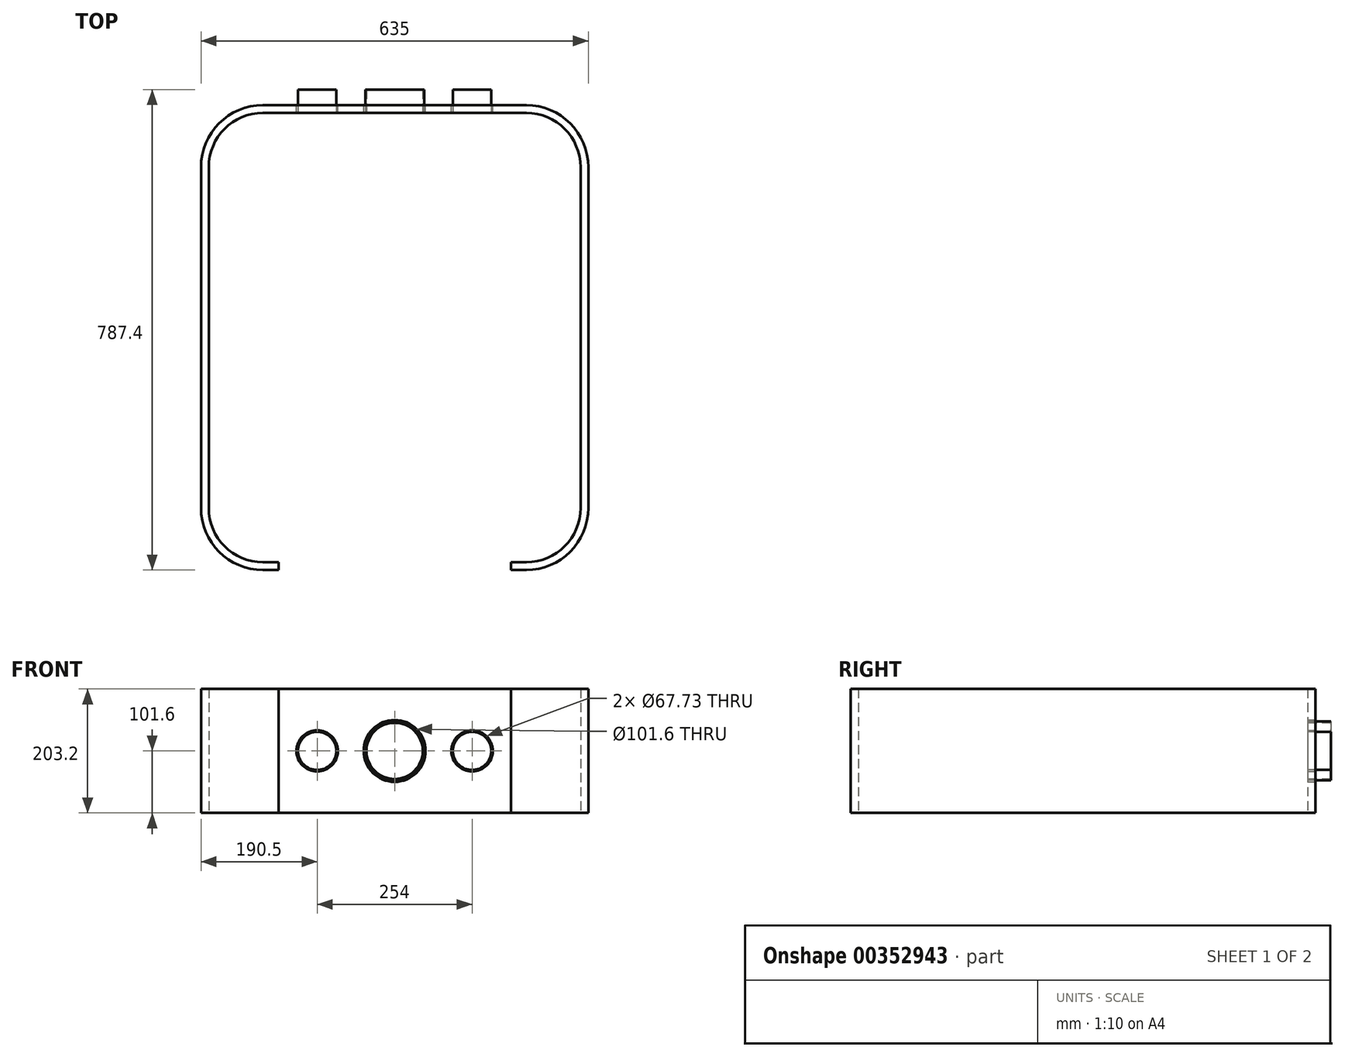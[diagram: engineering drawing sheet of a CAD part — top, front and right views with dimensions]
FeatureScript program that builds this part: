
annotation { "Feature Type Name" : "Feature", "Feature Type Description" : "" }
export const myFeature = defineFeature(function(context is Context, id is Id, definition is map)
    precondition{}
    {
        {
            var Q0;
            Q0=qCreatedBy(makeId("Top.planeOp"),FACE);
            var sketch = newSketch(context, id + "F0", { "sketchPlane" : qUnion([Q0])});
            skLineSegment(sketch, "E0.bottom", {"start": v(-215.9, -381) * mm, "end": v(-190.5, -381) * mm});
            skLineSegment(sketch, "E0.top", {"start": v(-215.9, 381) * mm, "end": v(215.9, 381) * mm});
            skLineSegment(sketch, "E0.left", {"start": v(-317.5, -279.4) * mm, "end": v(-317.5, 279.4) * mm});
            skLineSegment(sketch, "E0.right", {"start": v(317.5, -279.4) * mm, "end": v(317.5, 279.4) * mm});
            skPoint(sketch, "E0.middle", {"position": v(0, 0) * mm});
            skPoint(sketch, "E1.visualSharp", {"position": v(-317.5, 381) * mm});
            skArc(sketch, "E1.filletArc", {"start": v(-215.9, 381) * mm, "mid": v(-287.74, 351.24) * mm, "end": v(-317.5, 279.4) * mm});
            skPoint(sketch, "E2.visualSharp", {"position": v(317.5, 381) * mm});
            skArc(sketch, "E2.filletArc", {"start": v(317.5, 279.4) * mm, "mid": v(287.74, 351.24) * mm, "end": v(215.9, 381) * mm});
            skPoint(sketch, "E3.visualSharp", {"position": v(-317.5, -381) * mm});
            skArc(sketch, "E3.filletArc", {"start": v(-317.5, -279.4) * mm, "mid": v(-287.74, -351.24) * mm, "end": v(-215.9, -381) * mm});
            skPoint(sketch, "E4.visualSharp", {"position": v(317.5, -381) * mm});
            skArc(sketch, "E4.filletArc", {"start": v(215.9, -381) * mm, "mid": v(287.74, -351.24) * mm, "end": v(317.5, -279.4) * mm});
            skArc(sketch, "E5.0", {"start": v(215.9, -368.3) * mm, "mid": v(278.76, -342.26) * mm, "end": v(304.8, -279.4) * mm});
            skLineSegment(sketch, "E5.1", {"start": v(-215.9, -368.3) * mm, "end": v(-190.5, -368.3) * mm});
            skLineSegment(sketch, "E5.2", {"start": v(304.8, -279.4) * mm, "end": v(304.8, 279.4) * mm});
            skArc(sketch, "E5.3", {"start": v(-304.8, -279.4) * mm, "mid": v(-278.76, -342.26) * mm, "end": v(-215.9, -368.3) * mm});
            skArc(sketch, "E5.4", {"start": v(304.8, 279.4) * mm, "mid": v(278.76, 342.26) * mm, "end": v(215.9, 368.3) * mm});
            skLineSegment(sketch, "E5.5", {"start": v(-215.9, 368.3) * mm, "end": v(215.9, 368.3) * mm});
            skArc(sketch, "E5.6", {"start": v(-215.9, 368.3) * mm, "mid": v(-278.76, 342.26) * mm, "end": v(-304.8, 279.4) * mm});
            skLineSegment(sketch, "E5.7", {"start": v(-304.8, -279.4) * mm, "end": v(-304.8, 279.4) * mm});
            skLineSegment(sketch, "E6", {"start": v(-190.5, -368.3) * mm, "end": v(-190.5, -381) * mm});
            skLineSegment(sketch, "E7", {"start": v(0, 633.72) * mm, "end": v(0, -676.93) * mm, "construction": true});
            skPoint(sketch, "E7.endSnap0", {"position": v(0, -381) * mm});
            skLineSegment(sketch, "E8.MirrorCS", {"start": v(190.5, -368.3) * mm, "end": v(190.5, -381) * mm});
            skLineSegment(sketch, "E9.trimOffspring", {"start": v(190.5, -381) * mm, "end": v(215.9, -381) * mm});
            skLineSegment(sketch, "E10.trimOffspring", {"start": v(190.5, -368.3) * mm, "end": v(215.9, -368.3) * mm});
            skSolve(sketch);
        }
        {
            var Q0;
            Q0 = qSketchRegion(id + "F0", true);
            extrude(context, id + "F1", {"entities" : qUnion([Q0]), "depth" : 101.6 * mm, "hasSecondDirection" : true, "secondDirectionOppositeDirection" : true, "secondDirectionDepth" : 101.6 * mm});
        }
        {
            var Q0;
            Q0=makeQuery(id+"F1.opExtrude","SWEPT_FACE",FACE,{"disambiguationData":[OSD([sQuery(id+"F0.wireOp",EDGE,"E0.top")])]});
            var sketch = newSketch(context, id + "F2", { "sketchPlane" : qUnion([Q0])});
            skCircle(sketch, "E11", {"center": v(0, 0) * mm, "radius": 50.8 * mm});
            skCircle(sketch, "E12", {"center": v(-127, 0) * mm, "radius": 33.87 * mm});
            skLineSegment(sketch, "E13", {"start": v(0, 154.79) * mm, "end": v(0, -155.91) * mm, "construction": true});
            skPoint(sketch, "E13.endSnap0", {"position": v(0, -101.6) * mm});
            skCircle(sketch, "E14.MirrorC", {"center": v(127, 0) * mm, "radius": 33.87 * mm});
            skSolve(sketch);
        }
        {
            var Q0;
            Q0 = qSketchRegion(id + "F2", true);
            extrude(context, id + "F3", {"entities" : qUnion([Q0]), "operationType" : NewBodyOperationType.REMOVE, "oppositeDirection" : true, "depth" : 25.4 * mm});
        }
        {
            var Q0;
            Q0=makeQuery(id+"F1.opExtrude","SWEPT_FACE",FACE,{"disambiguationData":[OSD([sQuery(id+"F0.wireOp",EDGE,"E0.top")])]});
            var sketch = newSketch(context, id + "F4", { "sketchPlane" : qUnion([Q0])});
            skCircle(sketch, "E15", {"center": v(0, 0) * mm, "radius": 48.26 * mm});
            skCircle(sketch, "E16", {"center": v(0, 0) * mm, "radius": 46.34 * mm});
            skLineSegment(sketch, "E17", {"start": v(-193.05, 0) * mm, "end": v(205.45, 0) * mm, "construction": true});
            skCircle(sketch, "E18.0", {"center": v(-127, 0) * mm, "radius": 33.87 * mm, "construction": true});
            skCircle(sketch, "E19.0", {"center": v(127, 0) * mm, "radius": 33.87 * mm, "construction": true});
            skCircle(sketch, "E20", {"center": v(-127, 0) * mm, "radius": 31.33 * mm});
            skCircle(sketch, "E21", {"center": v(127, 0) * mm, "radius": 31.33 * mm});
            skSolve(sketch);
        }
        {
            var Q0;
            Q0 = qSketchRegion(id + "F4", true);
            var Q1;
            Q1=makeQuery(id+"F1.opExtrude","SWEPT_FACE",FACE,{"disambiguationData":[OSD([sQuery(id+"F0.wireOp",EDGE,"E5.5")])]});
            extrude(context, id + "F5", {"entities" : qUnion([Q0]), "depth" : 25.4 * mm, "hasSecondDirection" : true, "secondDirectionBound" : SecondDirectionBoundingType.UP_TO_SURFACE, "secondDirectionOppositeDirection" : true, "secondDirectionBoundEntityFace" : qUnion([Q1]), "secondDirectionDepth" : 25.4 * mm});
        }
        {
            var Q0;
            Q0=makeQuery(id+"F1.opExtrude","SWEPT_FACE",FACE,{"disambiguationData":[OSD([sQuery(id+"F0.wireOp",EDGE,"E0.top")])]});
            var sketch = newSketch(context, id + "F6", { "sketchPlane" : qUnion([Q0])});
            skCircle(sketch, "E22", {"center": v(0, 0) * mm, "radius": 46.08 * mm});
            skSolve(sketch);
        }
        {
            var Q0;
            Q0 = qSketchRegion(id + "F6", true);
            var Q1;
            Q1=makeQuery(id+"F1.opExtrude","SWEPT_FACE",FACE,{"disambiguationData":[OSD([sQuery(id+"F0.wireOp",EDGE,"E5.5")])]});
            extrude(context, id + "F7", {"entities" : qUnion([Q0]), "depth" : 25.4 * mm, "hasSecondDirection" : true, "secondDirectionBound" : SecondDirectionBoundingType.UP_TO_SURFACE, "secondDirectionOppositeDirection" : true, "secondDirectionBoundEntityFace" : qUnion([Q1]), "secondDirectionDepth" : 25.4 * mm});
        }
    });
